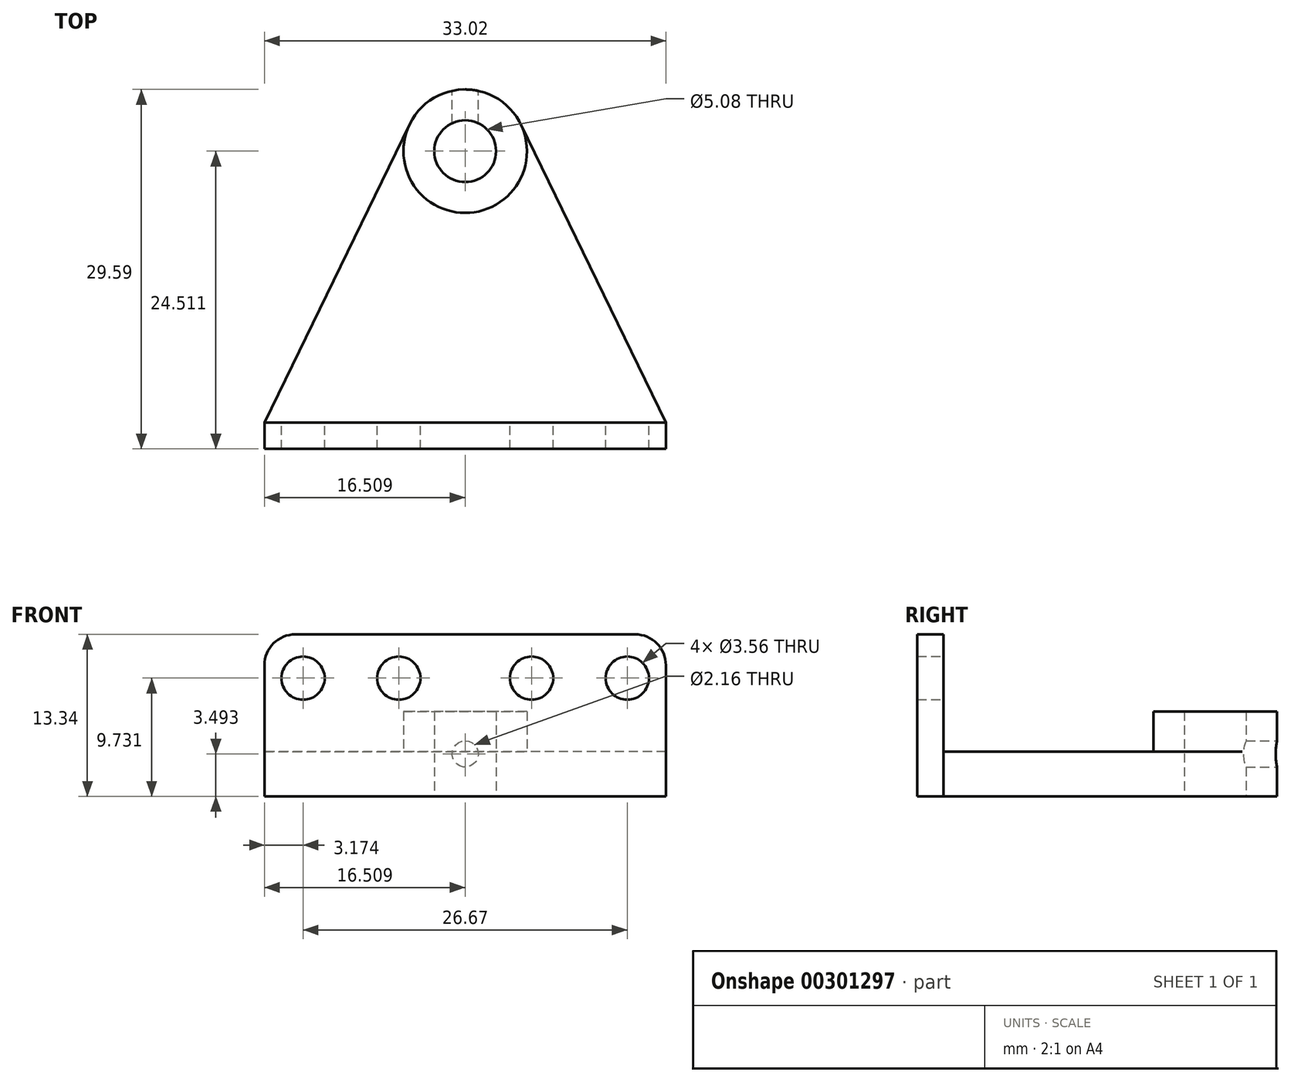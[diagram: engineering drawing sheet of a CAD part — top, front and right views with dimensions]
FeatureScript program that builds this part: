
annotation { "Feature Type Name" : "Feature", "Feature Type Description" : "" }
export const myFeature = defineFeature(function(context is Context, id is Id, definition is map)
    precondition{}
    {
        {
            var Q0;
            Q0=qCreatedBy(makeId("Top.planeOp"),FACE);
            var sketch = newSketch(context, id + "F0", { "sketchPlane" : qUnion([Q0])});
            skLineSegment(sketch, "E0.bottom", {"start": v(-4, 0) * mm, "end": v(29.03, 0) * mm});
            skLineSegment(sketch, "E0.top", {"start": v(-4, 2.16) * mm, "end": v(29.03, 2.16) * mm});
            skLineSegment(sketch, "E0.left", {"start": v(-4, 0) * mm, "end": v(-4, 2.16) * mm});
            skLineSegment(sketch, "E0.right", {"start": v(29.03, 0) * mm, "end": v(29.03, 2.16) * mm});
            skCircle(sketch, "E1", {"center": v(12.52, 24.51) * mm, "radius": 2.54 * mm});
            skPoint(sketch, "E1.centerSnap0", {"position": v(12.52, 2.16) * mm});
            skCircle(sketch, "E2", {"center": v(12.52, 24.51) * mm, "radius": 5.08 * mm});
            skLineSegment(sketch, "E3", {"start": v(-4, 2.16) * mm, "end": v(7.95, 26.73) * mm});
            skLineSegment(sketch, "E4", {"start": v(29.03, 2.16) * mm, "end": v(17.09, 26.73) * mm});
            skSolve(sketch);
        }
        {
            var Q0;
            Q0=makeQuery(id+"F0.imprint","IMPRINT",FACE,{"disambiguationData":[TD([[makeQuery(id+"F0.imprint","IMPRINT",EDGE,{"derivedFrom":sQuery(id+"F0.wireOp",EDGE,"E0.bottom")}),1.0]])]});
            var Q1;
            Q1=makeQuery(id+"F0.imprint","IMPRINT",FACE,{"disambiguationData":[TD([[makeQuery(id+"F0.imprint","IMPRINT",EDGE,{"derivedFrom":sQuery(id+"F0.wireOp",EDGE,"E0.top")}),1.0]])]});
            var Q2;
            Q2=makeQuery(id+"F0.imprint","IMPRINT",FACE,{"disambiguationData":[TD([[makeQuery(id+"F0.imprint","IMPRINT",EDGE,{"derivedFrom":sQuery(id+"F0.wireOp",EDGE,"E1")}),-1.0]])]});
            extrude(context, id + "F1", {"entities" : qUnion([Q0, Q1, Q2]), "depth" : 3.68 * mm});
        }
        {
            var Q0;
            Q0=makeQuery(id+"F0.imprint","IMPRINT",FACE,{"disambiguationData":[TD([[makeQuery(id+"F0.imprint","IMPRINT",EDGE,{"derivedFrom":sQuery(id+"F0.wireOp",EDGE,"E0.bottom")}),1.0]])]});
            extrude(context, id + "F2", {"entities" : qUnion([Q0]), "operationType" : NewBodyOperationType.ADD, "depth" : 13.33 * mm});
        }
        {
            var Q0;
            Q0=makeQuery(id+"F0.imprint","IMPRINT",FACE,{"disambiguationData":[TD([[makeQuery(id+"F0.imprint","IMPRINT",EDGE,{"derivedFrom":sQuery(id+"F0.wireOp",EDGE,"E1")}),-1.0]])]});
            extrude(context, id + "F3", {"entities" : qUnion([Q0]), "operationType" : NewBodyOperationType.ADD, "depth" : 7 * mm});
        }
        {
            var Q0;
            Q0=makeQuery(id+"F2.opExtrude","SWEPT_FACE",FACE,{"disambiguationData":[OSD([sQuery(id+"F0.wireOp",EDGE,"E0.top")])]});
            var sketch = newSketch(context, id + "F4", { "sketchPlane" : qUnion([Q0])});
            skCircle(sketch, "E5", {"center": v(0.82, 9.73) * mm, "radius": 1.78 * mm});
            skCircle(sketch, "E6", {"center": v(-25.85, 9.73) * mm, "radius": 1.78 * mm});
            skCircle(sketch, "E7", {"center": v(-17.98, 9.73) * mm, "radius": 1.78 * mm});
            skCircle(sketch, "E8", {"center": v(-7.06, 9.73) * mm, "radius": 1.78 * mm});
            skSolve(sketch);
        }
        {
            var Q0;
            Q0=qSketchRegion(id+"F4",true);
            extrude(context, id + "F5", {"entities" : qUnion([Q0]), "operationType" : NewBodyOperationType.REMOVE, "oppositeDirection" : true, "depth" : 25.4 * mm});
        }
        {
            var Q0;
            Q0=makeQuery(id+"F2.opExtrude","CAP_EDGE",EDGE,{"disambiguationData":[OSD([sQuery(id+"F0.wireOp",EDGE,"E0.left")])],"isStart":false});
            var Q1;
            Q1=makeQuery(id+"F2.opExtrude","CAP_EDGE",EDGE,{"disambiguationData":[OSD([sQuery(id+"F0.wireOp",EDGE,"E0.right")])],"isStart":false});
            fillet(context, id + "F6", {"entities" : qUnion([Q0, Q1]), "radius" : 2.54 * mm, "tangentPropagation" : true, "allowEdgeOverflow" : false});
        }
        {
            var Q0;
            Q0=qCreatedBy(makeId("Front.planeOp"),FACE);
            cPlane(context, id + "F7", {"entities" : qUnion([Q0]), "cplaneType" : CPlaneType.OFFSET, "offset" : 29.6 * mm, "oppositeDirection" : true, "width" : 152.4 * mm, "height" : 152.4 * mm});
        }
        {
            var Q0;
            Q0=qCreatedBy(id+"F7.planeOp",FACE);
            var sketch = newSketch(context, id + "F8", { "sketchPlane" : qUnion([Q0])});
            skLineSegment(sketch, "E9.0", {"start": v(17.09, 0) * mm, "end": v(7.95, 0) * mm});
            skPoint(sketch, "E10", {"position": v(12.52, 0) * mm});
            skCircle(sketch, "E11", {"center": v(12.52, 3.5) * mm, "radius": 1.08 * mm});
            skSolve(sketch);
        }
        {
            var Q0;
            Q0=qSketchRegion(id+"F8",true);
            extrude(context, id + "F9", {"entities" : qUnion([Q0]), "operationType" : NewBodyOperationType.REMOVE, "depth" : 3.8 * mm});
        }
    });
